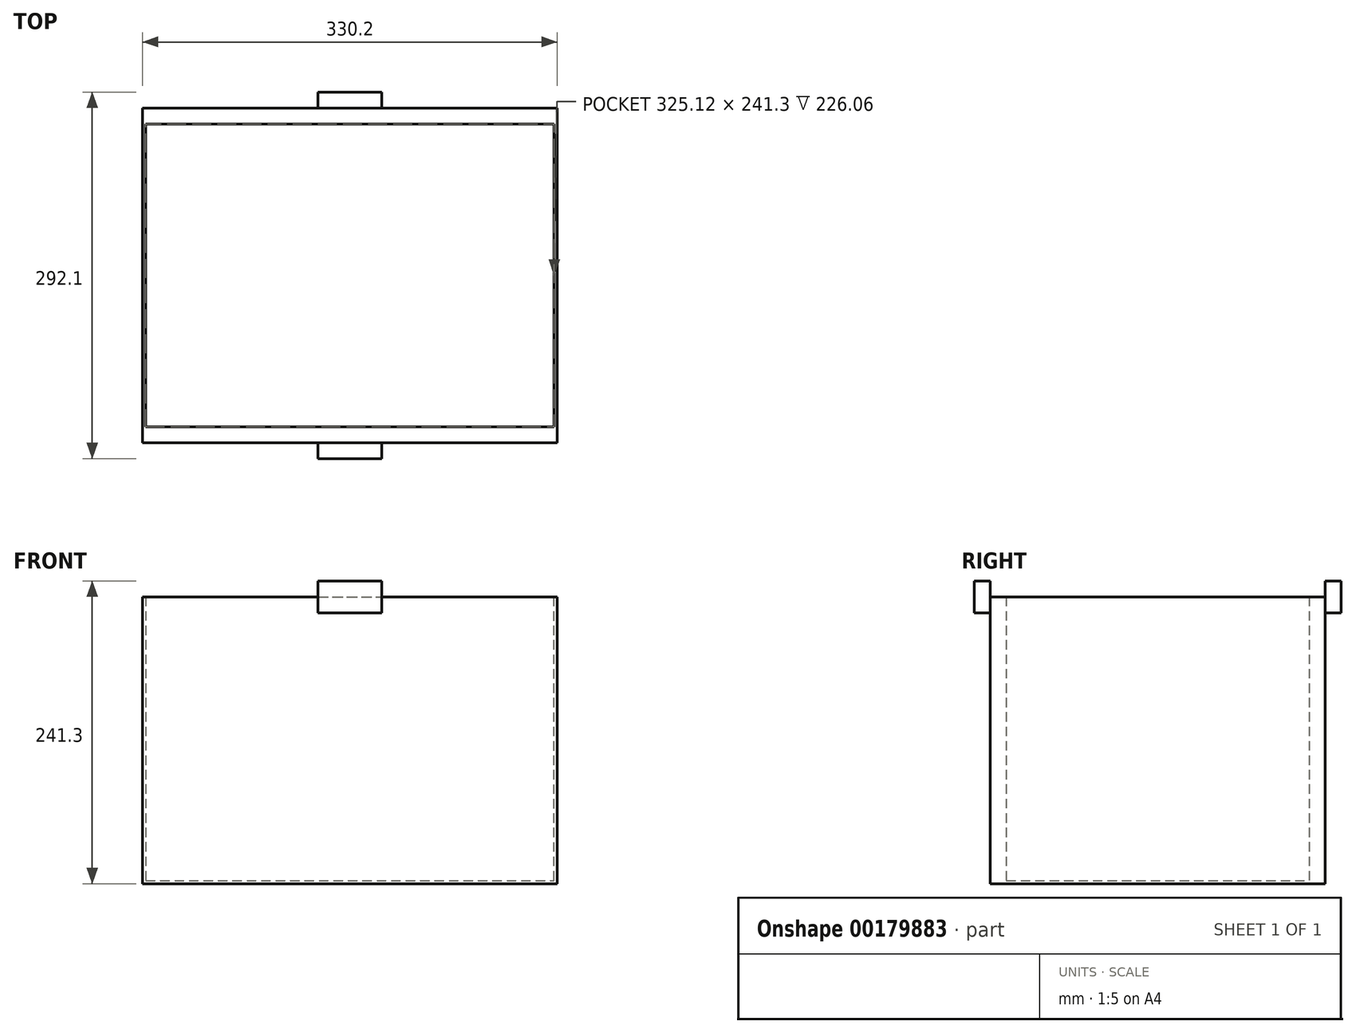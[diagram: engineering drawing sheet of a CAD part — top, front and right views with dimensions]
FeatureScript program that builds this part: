
annotation { "Feature Type Name" : "Feature", "Feature Type Description" : "" }
export const myFeature = defineFeature(function(context is Context, id is Id, definition is map)
    precondition{}
    {
        {
            var Q0;
            Q0=qCreatedBy(makeId("Front.planeOp"),FACE);
            var sketch = newSketch(context, id + "F0", { "sketchPlane" : qUnion([Q0])});
            skLineSegment(sketch, "E0.bottom", {"start": v(-165.1, 114.3) * mm, "end": v(165.1, 114.3) * mm});
            skLineSegment(sketch, "E0.top", {"start": v(-165.1, -114.3) * mm, "end": v(165.1, -114.3) * mm});
            skLineSegment(sketch, "E0.left", {"start": v(-165.1, 114.3) * mm, "end": v(-165.1, -114.3) * mm});
            skLineSegment(sketch, "E0.right", {"start": v(165.1, 114.3) * mm, "end": v(165.1, -114.3) * mm});
            skPoint(sketch, "E0.middle", {"position": v(0, 0) * mm});
            skSolve(sketch);
        }
        {
            var Q0;
            Q0=makeQuery(id+"F0.imprint","IMPRINT",FACE,{"disambiguationData":[TD([[makeQuery(id+"F0.imprint","IMPRINT",EDGE,{"derivedFrom":sQuery(id+"F0.wireOp",EDGE,"E0.bottom")}),-1.0]])]});
            extrude(context, id + "F1", {"entities" : qUnion([Q0]), "depth" : 12.7 * mm});
        }
        {
            var Q0;
            Q0=makeQuery(id+"F1.opExtrude","CAP_FACE",FACE,{"disambiguationData":[OSD([sQuery(id+"F0.wireOp",EDGE,"E0.bottom"),sQuery(id+"F0.wireOp",EDGE,"E0.top"),sQuery(id+"F0.wireOp",EDGE,"E0.left"),sQuery(id+"F0.wireOp",EDGE,"E0.right")])],"isStart":false});
            var sketch = newSketch(context, id + "F2", { "sketchPlane" : qUnion([Q0])});
            skLineSegment(sketch, "E1", {"start": v(-162.56, 114.3) * mm, "end": v(-162.56, -111.76) * mm});
            skLineSegment(sketch, "E2", {"start": v(-162.56, -111.76) * mm, "end": v(162.56, -111.76) * mm});
            skLineSegment(sketch, "E3", {"start": v(162.56, -111.76) * mm, "end": v(162.56, 114.3) * mm});
            skSolve(sketch);
        }
        {
            var Q0;
            {var subQ1=sQuery(id+"F2.wireOp",EDGE,"E1");Q0=makeQuery(id+"F2.imprint","IMPRINT",FACE,{"disambiguationData":[TD([[makeQuery(id+"F2.imprint","IMPRINT",EDGE,{"derivedFrom":subQ1}),-1.0]])]});}
            extrude(context, id + "F3", {"entities" : qUnion([Q0]), "operationType" : NewBodyOperationType.ADD, "depth" : 241.3 * mm});
        }
        {
            var Q0;
            Q0=makeQuery(id+"F3.opExtrude","CAP_FACE",FACE,{"disambiguationData":[OSD([sQuery(id+"F0.wireOp",EDGE,"E0.bottom"),sQuery(id+"F0.wireOp",EDGE,"E0.top"),sQuery(id+"F0.wireOp",EDGE,"E0.left"),sQuery(id+"F0.wireOp",EDGE,"E0.right"),sQuery(id+"F2.wireOp",EDGE,"E1"),sQuery(id+"F2.wireOp",EDGE,"E2"),sQuery(id+"F2.wireOp",EDGE,"E3")])],"isStart":false});
            var sketch = newSketch(context, id + "F4", { "sketchPlane" : qUnion([Q0])});
            skLineSegment(sketch, "E4", {"start": v(-165.1, 114.3) * mm, "end": v(165.1, 114.3) * mm});
            skLineSegment(sketch, "E5", {"start": v(165.1, 114.3) * mm, "end": v(165.1, -114.3) * mm});
            skLineSegment(sketch, "E6", {"start": v(165.1, -114.3) * mm, "end": v(-165.1, -114.3) * mm});
            skLineSegment(sketch, "E7", {"start": v(-165.1, -114.3) * mm, "end": v(-165.1, 114.3) * mm});
            skSolve(sketch);
        }
        {
            var Q0;
            {var subQ1=makeQuery(id+"F3.opExtrude","CAP_EDGE",EDGE,{"disambiguationData":[OSD([sQuery(id+"F2.wireOp",EDGE,"E1")])],"isStart":false});Q0=makeQuery(id+"F4.imprint","IMPRINT",FACE,{"disambiguationData":[TD([[makeQuery(id+"F4.imprint","IMPRINT",EDGE,{"derivedFrom":subQ1}),1.0]])]});}
            var Q1;
            {var subQ3=sQuery(id+"F4.wireOp",EDGE,"E5");Q1=makeQuery(id+"F4.imprint","IMPRINT",FACE,{"disambiguationData":[TD([[makeQuery(id+"F4.imprint","IMPRINT",EDGE,{"derivedFrom":subQ3}),-1.0]])]});}
            extrude(context, id + "F5", {"entities" : qUnion([Q0, Q1]), "operationType" : NewBodyOperationType.ADD, "depth" : 12.7 * mm});
        }
        {
            var Q0;
            Q0=makeQuery(id+"F5.opExtrude","CAP_FACE",FACE,{"disambiguationData":[OSD([sQuery(id+"F4.wireOp",EDGE,"E4"),sQuery(id+"F4.wireOp",EDGE,"E5"),sQuery(id+"F4.wireOp",EDGE,"E6"),sQuery(id+"F4.wireOp",EDGE,"E7")])],"isStart":false});
            var sketch = newSketch(context, id + "F6", { "sketchPlane" : qUnion([Q0])});
            skLineSegment(sketch, "E8", {"start": v(-25.4, 127) * mm, "end": v(-25.4, 101.6) * mm});
            skLineSegment(sketch, "E9", {"start": v(-25.4, 101.6) * mm, "end": v(25.4, 101.6) * mm});
            skLineSegment(sketch, "E10", {"start": v(25.4, 101.6) * mm, "end": v(25.4, 127) * mm});
            skLineSegment(sketch, "E11", {"start": v(25.4, 127) * mm, "end": v(-25.4, 127) * mm});
            skSolve(sketch);
        }
        {
            var Q0;
            {var subQ0=sQuery(id+"F6.wireOp",EDGE,"E11");Q0=makeQuery(id+"F6.imprint","IMPRINT",FACE,{"disambiguationData":[TD([[makeQuery(id+"F6.imprint","IMPRINT",EDGE,{"derivedFrom":subQ0}),1.0]])]});}
            var Q1;
            {var subQ0=sQuery(id+"F6.wireOp",EDGE,"E9");Q1=makeQuery(id+"F6.imprint","IMPRINT",FACE,{"disambiguationData":[TD([[makeQuery(id+"F6.imprint","IMPRINT",EDGE,{"derivedFrom":subQ0}),1.0]])]});}
            extrude(context, id + "F7", {"entities" : qUnion([Q0, Q1]), "operationType" : NewBodyOperationType.ADD, "depth" : 12.7 * mm});
        }
        {
            var Q0;
            Q0=makeQuery(id+"F1.opExtrude","CAP_FACE",FACE,{"disambiguationData":[OSD([sQuery(id+"F0.wireOp",EDGE,"E0.bottom"),sQuery(id+"F0.wireOp",EDGE,"E0.top"),sQuery(id+"F0.wireOp",EDGE,"E0.left"),sQuery(id+"F0.wireOp",EDGE,"E0.right")])],"isStart":true});
            var sketch = newSketch(context, id + "F8", { "sketchPlane" : qUnion([Q0])});
            skLineSegment(sketch, "E12", {"start": v(-25.4, 127) * mm, "end": v(-25.4, 101.6) * mm});
            skLineSegment(sketch, "E13", {"start": v(-25.4, 101.6) * mm, "end": v(25.4, 101.6) * mm});
            skLineSegment(sketch, "E14", {"start": v(25.4, 101.6) * mm, "end": v(25.4, 127) * mm});
            skLineSegment(sketch, "E15", {"start": v(25.4, 127) * mm, "end": v(-25.4, 127) * mm});
            skSolve(sketch);
        }
        {
            var Q0;
            {var subQ0=sQuery(id+"F8.wireOp",EDGE,"E13");Q0=makeQuery(id+"F8.imprint","IMPRINT",FACE,{"disambiguationData":[TD([[makeQuery(id+"F8.imprint","IMPRINT",EDGE,{"derivedFrom":subQ0}),1.0]])]});}
            var Q1;
            {var subQ0=sQuery(id+"F8.wireOp",EDGE,"E15");Q1=makeQuery(id+"F8.imprint","IMPRINT",FACE,{"disambiguationData":[TD([[makeQuery(id+"F8.imprint","IMPRINT",EDGE,{"derivedFrom":subQ0}),1.0]])]});}
            extrude(context, id + "F9", {"entities" : qUnion([Q0, Q1]), "operationType" : NewBodyOperationType.ADD, "depth" : 12.7 * mm});
        }
    });
